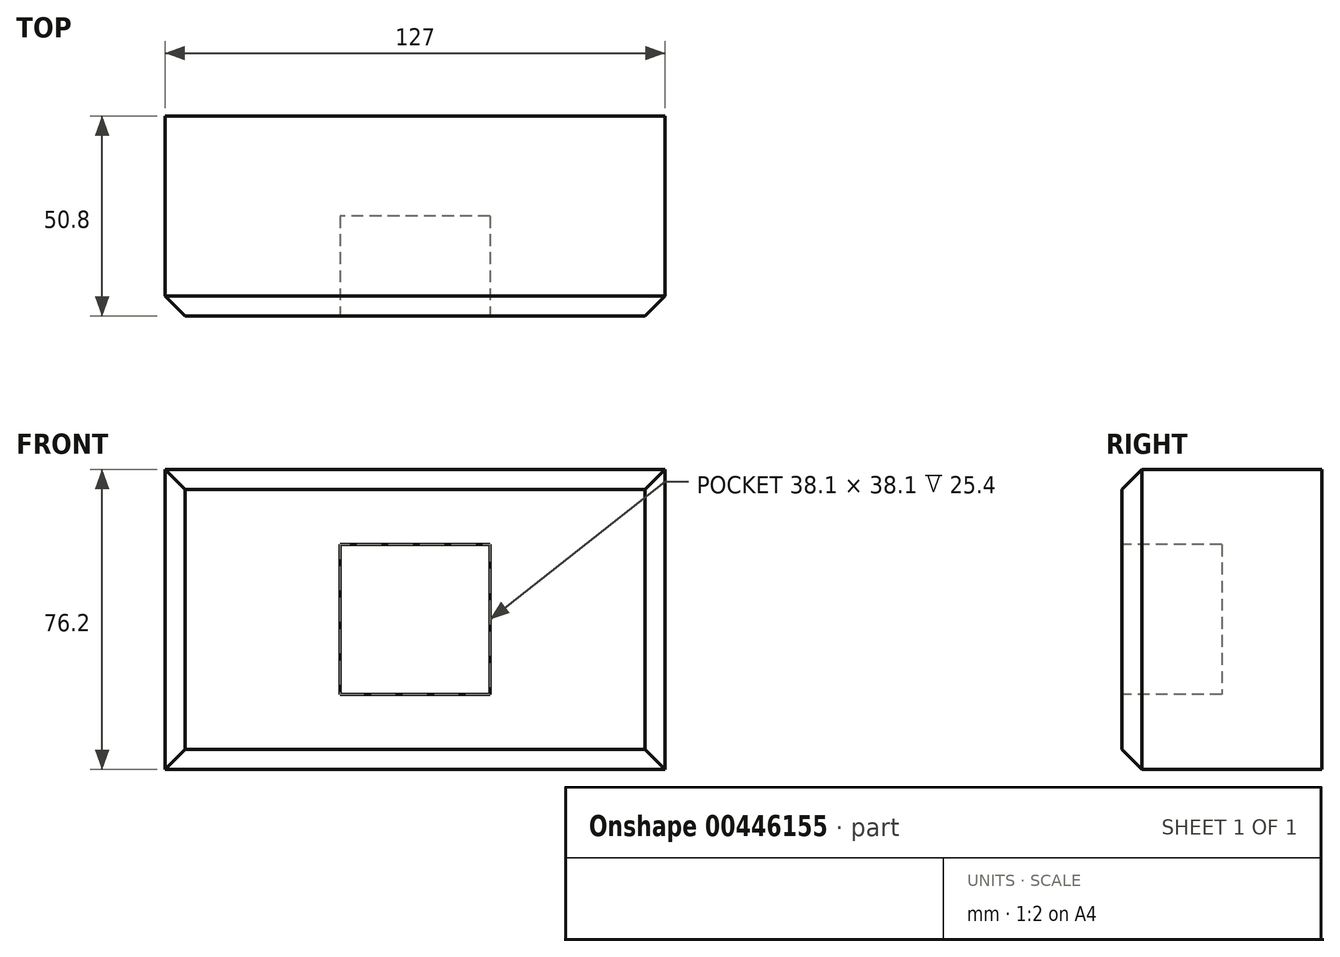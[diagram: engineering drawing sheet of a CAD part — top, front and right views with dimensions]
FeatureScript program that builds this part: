
annotation { "Feature Type Name" : "Feature", "Feature Type Description" : "" }
export const myFeature = defineFeature(function(context is Context, id is Id, definition is map)
    precondition{}
    {
        {
            var Q0;
            Q0=qCreatedBy(makeId("Front.planeOp"),FACE);
            var sketch = newSketch(context, id + "F0", { "sketchPlane" : qUnion([Q0])});
            skLineSegment(sketch, "E0.bottom", {"start": v(-68.81, 26.65) * mm, "end": v(58.19, 26.65) * mm});
            skLineSegment(sketch, "E0.top", {"start": v(-68.81, -49.55) * mm, "end": v(58.19, -49.55) * mm});
            skLineSegment(sketch, "E0.left", {"start": v(-68.81, 26.65) * mm, "end": v(-68.81, -49.55) * mm});
            skLineSegment(sketch, "E0.right", {"start": v(58.19, 26.65) * mm, "end": v(58.19, -49.55) * mm});
            skSolve(sketch);
        }
        {
            var Q0;
            Q0=makeQuery(id+"F0.imprint","IMPRINT",FACE,{"disambiguationData":[TD([[makeQuery(id+"F0.imprint","IMPRINT",EDGE,{"derivedFrom":sQuery(id+"F0.wireOp",EDGE,"E0.bottom")}),-1.0]])]});
            extrude(context, id + "F1", {"entities" : qUnion([Q0]), "depth" : 50.8 * mm});
        }
        {
            var Q0;
            Q0=makeQuery(id+"F1.opExtrude","CAP_FACE",FACE,{"disambiguationData":[OSD([sQuery(id+"F0.wireOp",EDGE,"E0.bottom"),sQuery(id+"F0.wireOp",EDGE,"E0.top"),sQuery(id+"F0.wireOp",EDGE,"E0.left"),sQuery(id+"F0.wireOp",EDGE,"E0.right")])],"isStart":false});
            var sketch = newSketch(context, id + "F2", { "sketchPlane" : qUnion([Q0])});
            skLineSegment(sketch, "E1.bottom", {"start": v(13.74, 7.6) * mm, "end": v(-24.36, 7.6) * mm});
            skLineSegment(sketch, "E1.top", {"start": v(13.74, -30.5) * mm, "end": v(-24.36, -30.5) * mm});
            skLineSegment(sketch, "E1.left", {"start": v(13.74, 7.6) * mm, "end": v(13.74, -30.5) * mm});
            skLineSegment(sketch, "E1.right", {"start": v(-24.36, 7.6) * mm, "end": v(-24.36, -30.5) * mm});
            skPoint(sketch, "E1.middle", {"position": v(-5.31, -11.45) * mm});
            skPoint(sketch, "E1.middle.positionSnap0", {"position": v(-5.31, -49.55) * mm});
            skPoint(sketch, "E1.middle.positionSnap1", {"position": v(-68.81, -11.45) * mm});
            skPoint(sketch, "E1.centerSnap0", {"position": v(-5.31, -49.55) * mm});
            skPoint(sketch, "E1.centerSnap1", {"position": v(-68.81, -11.45) * mm});
            skSolve(sketch);
        }
        {
            var Q0;
            Q0=makeQuery(id+"F2.imprint","IMPRINT",FACE,{"disambiguationData":[TD([[makeQuery(id+"F2.imprint","IMPRINT",EDGE,{"derivedFrom":sQuery(id+"F2.wireOp",EDGE,"E1.bottom")}),1.0]])]});
            extrude(context, id + "F3", {"entities" : qUnion([Q0]), "operationType" : NewBodyOperationType.REMOVE, "oppositeDirection" : true, "depth" : 25.4 * mm});
        }
        {
            var Q0;
            Q0=makeQuery(id+"F1.opExtrude","CAP_EDGE",EDGE,{"disambiguationData":[OSD([sQuery(id+"F0.wireOp",EDGE,"E0.bottom")])],"isStart":false});
            var Q1;
            Q1=makeQuery(id+"F1.opExtrude","CAP_EDGE",EDGE,{"disambiguationData":[OSD([sQuery(id+"F0.wireOp",EDGE,"E0.right")])],"isStart":false});
            var Q2;
            Q2=makeQuery(id+"F1.opExtrude","CAP_EDGE",EDGE,{"disambiguationData":[OSD([sQuery(id+"F0.wireOp",EDGE,"E0.top")])],"isStart":false});
            var Q3;
            Q3=makeQuery(id+"F1.opExtrude","CAP_EDGE",EDGE,{"disambiguationData":[OSD([sQuery(id+"F0.wireOp",EDGE,"E0.left")])],"isStart":false});
            chamfer(context, id + "F4", {"entities" : qUnion([Q0, Q1, Q2, Q3]), "width" : 5.08 * mm, "tangentPropagation" : true});
        }
    });
